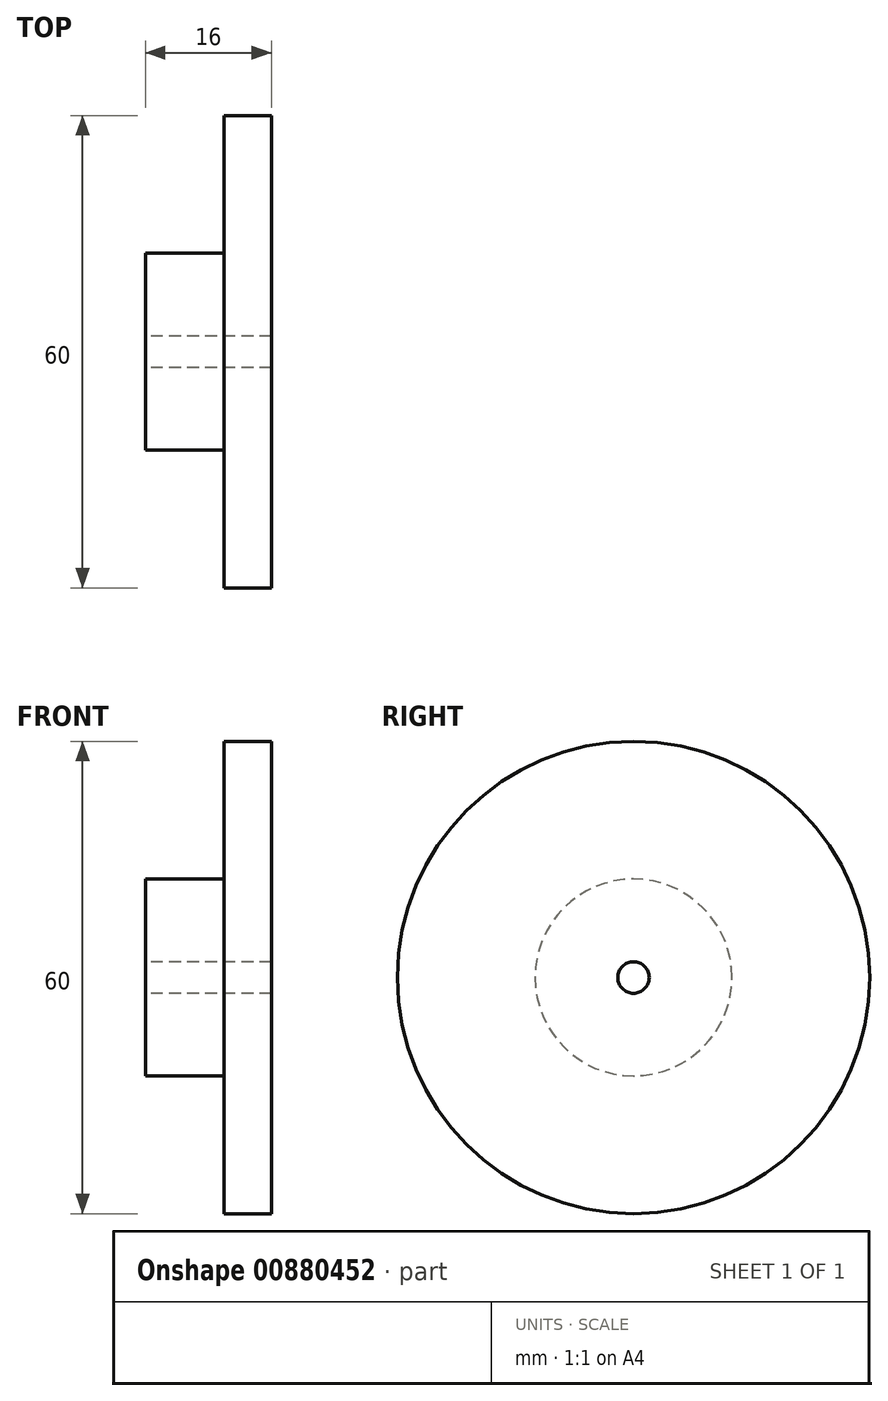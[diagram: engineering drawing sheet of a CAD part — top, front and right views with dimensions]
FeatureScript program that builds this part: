
annotation { "Feature Type Name" : "Feature", "Feature Type Description" : "" }
export const myFeature = defineFeature(function(context is Context, id is Id, definition is map)
    precondition{}
    {
        {
            var Q0;
            Q0=qCreatedBy(makeId("Right.planeOp"),FACE);
            var sketch = newSketch(context, id + "F0", { "sketchPlane" : qUnion([Q0])});
            skCircle(sketch, "E0", {"center": v(0, 0) * mm, "radius": 30 * mm});
            skCircle(sketch, "E1", {"center": v(0, 0) * mm, "radius": 2 * mm});
            skSolve(sketch);
        }
        {
            var Q0;
            Q0 = qSketchRegion(id + "F0", true);
            extrude(context, id + "F1", {"entities" : qUnion([Q0]), "depth" : 6 * mm, "offsetDistance" : 25 * mm});
        }
        {
            var Q0;
            Q0=qCreatedBy(makeId("Right.planeOp"),FACE);
            var sketch = newSketch(context, id + "F2", { "sketchPlane" : qUnion([Q0])});
            skCircle(sketch, "E2", {"center": v(0, 0) * mm, "radius": 12.5 * mm});
            skCircle(sketch, "E3", {"center": v(0, 0) * mm, "radius": 2 * mm});
            skSolve(sketch);
        }
        {
            var Q0;
            Q0 = qSketchRegion(id + "F2", true);
            extrude(context, id + "F3", {"entities" : qUnion([Q0]), "operationType" : NewBodyOperationType.ADD, "oppositeDirection" : true, "depth" : 10 * mm, "offsetDistance" : 25 * mm});
        }
    });
